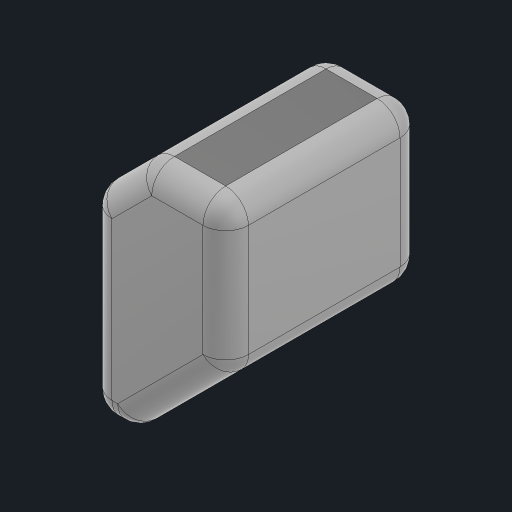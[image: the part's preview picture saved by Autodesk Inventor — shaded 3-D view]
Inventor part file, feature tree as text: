
AUTODESK INVENTOR PART (.ipt)
format: ipt  version: 2023.2 (Build 272271030, 271C)  size: 165,888 bytes
history: native  units: mm
features: extrude x2, chamfer x2, sketch x2, fillet x1, projected_geometry x1
ambient origin geometry x8: Origin, YZ Plane, XZ Plane, XY Plane, X Axis, Y Axis, Z Axis, Center Point
bodies: Solid1 (feature_tree)
feature tree (8):
  extrude  "Extrusion1"  Depth=32.0mm
  chamfer  "Chamfer1"  Distance=26.0mm
  chamfer  "Chamfer2"  Distance=7.0mm Angle=45.0deg
  fillet  "Fillet1"  Radius=3.0mm
  extrude  "Extrusion2"  Depth=20.0mm TaperAngle=0.0deg
  sketch  "Sketch1"  dims[d0=18.0mm d1=32.0mm d2=26.0mm d3=0.0mm d4=7.0mm d5=2.0mm d6=45.0deg]
  sketch  "Sketch2"  dims[d7=13.0mm d8=2.0mm d9=45.0deg d10=3.0mm d11=20.0mm d12=0.0mm]
  projected_geometry  "Projected Loop1"
